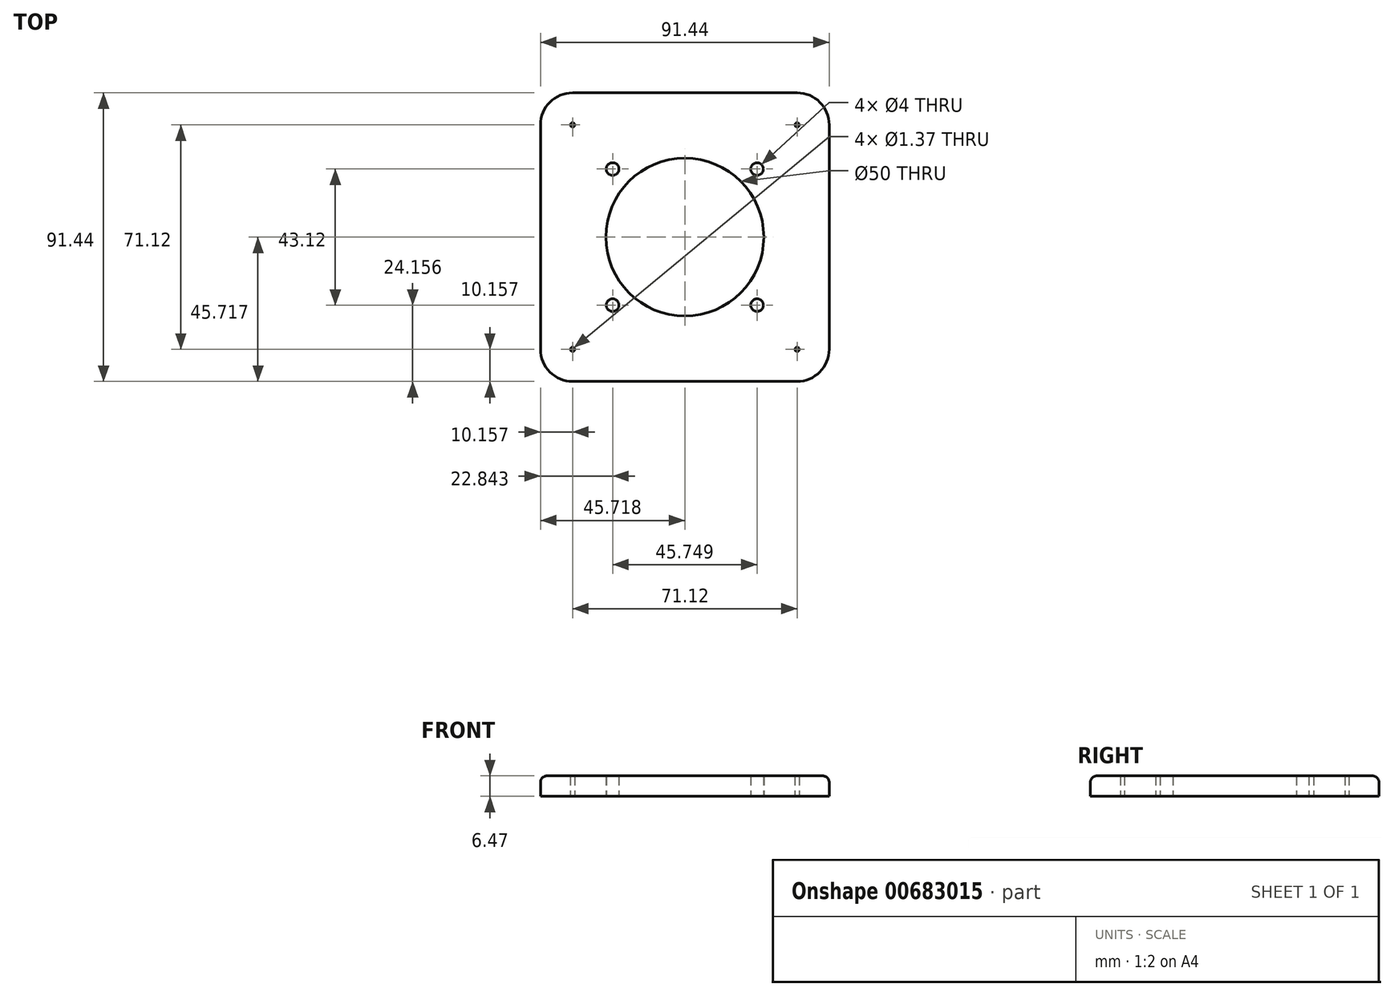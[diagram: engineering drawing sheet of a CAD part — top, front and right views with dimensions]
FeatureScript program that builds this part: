
annotation { "Feature Type Name" : "Feature", "Feature Type Description" : "" }
export const myFeature = defineFeature(function(context is Context, id is Id, definition is map)
    precondition{}
    {
        {
            var Q0;
            Q0=qCreatedBy(makeId("Top.planeOp"),FACE);
            var sketch = newSketch(context, id + "F0", { "sketchPlane" : qUnion([Q0])});
            skCircle(sketch, "E0", {"center": v(0, -0.1) * mm, "radius": 25 * mm});
            skCircle(sketch, "E1", {"center": v(-22.87, 21.47) * mm, "radius": 2 * mm});
            skCircle(sketch, "E2", {"center": v(22.88, 21.47) * mm, "radius": 2 * mm});
            skCircle(sketch, "E3", {"center": v(22.88, -21.65) * mm, "radius": 2 * mm});
            skCircle(sketch, "E4", {"center": v(-22.87, -21.65) * mm, "radius": 2 * mm});
            skCircle(sketch, "E5", {"center": v(-35.55, 35.47) * mm, "radius": 0.69 * mm});
            skCircle(sketch, "E6", {"center": v(35.57, 35.47) * mm, "radius": 0.69 * mm});
            skCircle(sketch, "E7", {"center": v(-35.55, -35.65) * mm, "radius": 0.69 * mm});
            skCircle(sketch, "E8", {"center": v(35.57, -35.65) * mm, "radius": 0.69 * mm});
            skArc(sketch, "E9", {"start": v(-35.55, 45.63) * mm, "mid": v(-42.74, 42.65) * mm, "end": v(-45.71, 35.47) * mm});
            skArc(sketch, "E10", {"start": v(45.73, 35.47) * mm, "mid": v(42.75, 42.65) * mm, "end": v(35.57, 45.63) * mm});
            skArc(sketch, "E11", {"start": v(-45.71, -35.65) * mm, "mid": v(-42.74, -42.84) * mm, "end": v(-35.55, -45.81) * mm});
            skArc(sketch, "E12", {"start": v(35.57, -45.81) * mm, "mid": v(42.75, -42.84) * mm, "end": v(45.73, -35.65) * mm});
            skLineSegment(sketch, "E13", {"start": v(-35.55, 45.63) * mm, "end": v(35.57, 45.63) * mm});
            skLineSegment(sketch, "E14", {"start": v(-45.71, 35.47) * mm, "end": v(-45.71, -35.65) * mm});
            skLineSegment(sketch, "E15", {"start": v(-35.55, -45.81) * mm, "end": v(35.57, -45.81) * mm});
            skLineSegment(sketch, "E16", {"start": v(45.73, -35.65) * mm, "end": v(45.73, 35.47) * mm});
            skSolve(sketch);
        }
        {
            var Q0;
            Q0=makeQuery(id+"F0.imprint","IMPRINT",FACE,{"disambiguationData":[TD([[makeQuery(id+"F0.imprint","IMPRINT",EDGE,{"derivedFrom":sQuery(id+"F0.wireOp",EDGE,"E0")}),-1.0]])]});
            extrude(context, id + "F1", {"entities" : qUnion([Q0]), "depth" : 6.47 * mm, "offsetDistance" : 25.4 * mm});
        }
        {
            var Q0;
            Q0=makeQuery(id+"F1.opExtrude","CAP_EDGE",EDGE,{"disambiguationData":[OSD([sQuery(id+"F0.wireOp",EDGE,"E14")])],"isStart":false});
            fillet(context, id + "F2", {"entities" : qUnion([Q0]), "radius" : 2.03 * mm, "tangentPropagation" : true, "allowEdgeOverflow" : false});
        }
    });
